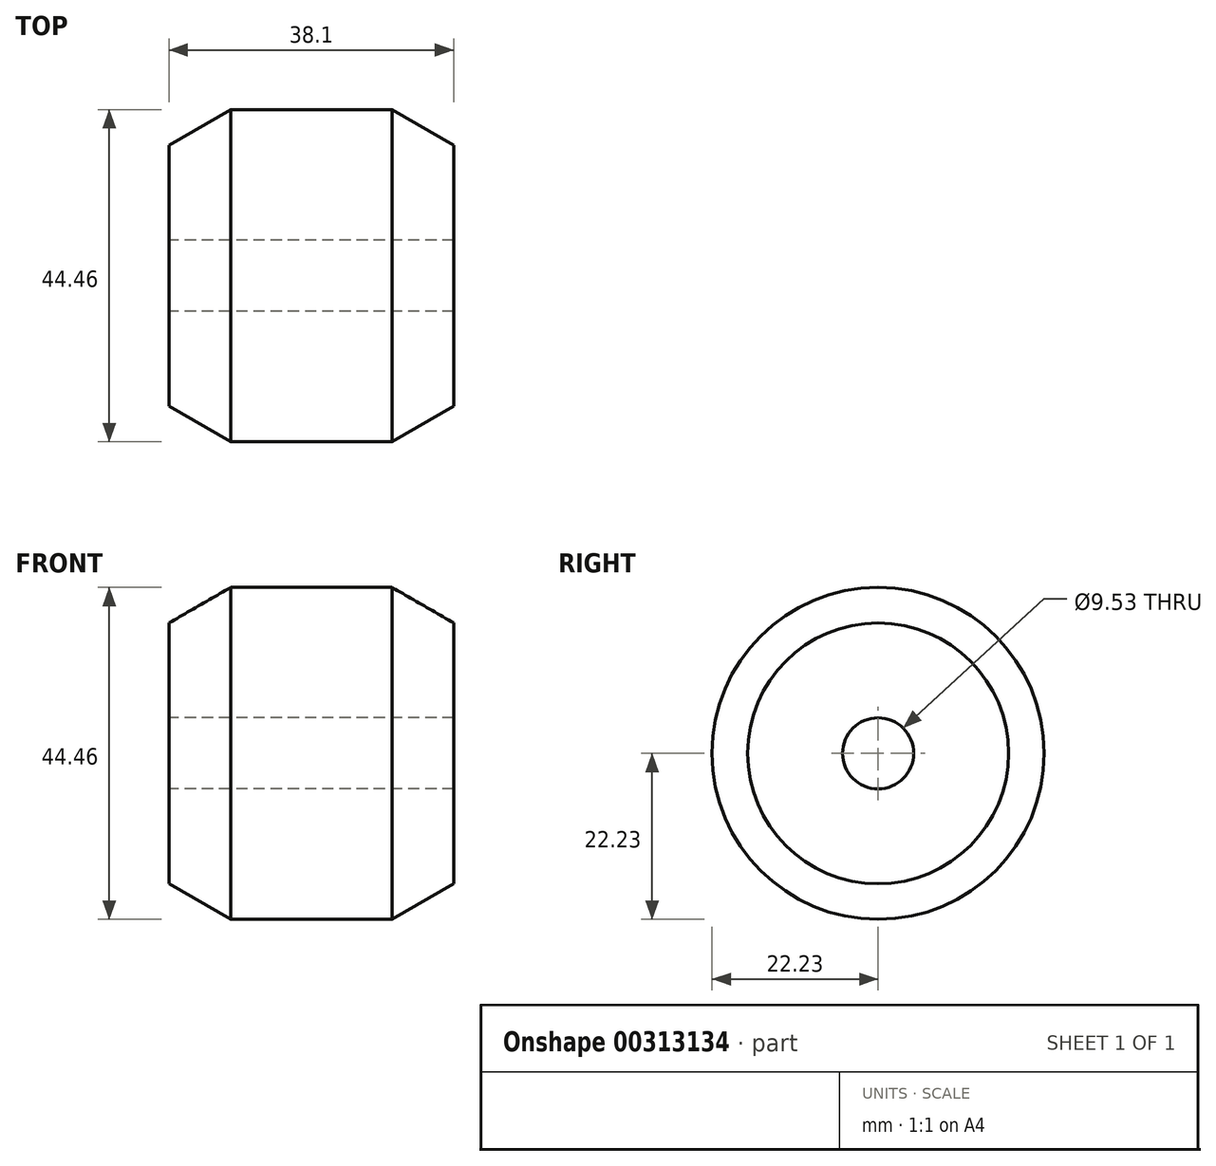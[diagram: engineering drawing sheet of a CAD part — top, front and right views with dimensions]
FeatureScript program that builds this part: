
annotation { "Feature Type Name" : "Feature", "Feature Type Description" : "" }
export const myFeature = defineFeature(function(context is Context, id is Id, definition is map)
    precondition{}
    {
        {
            var Q0;
            Q0=qCreatedBy(makeId("Front.planeOp"),FACE);
            var sketch = newSketch(context, id + "F0", { "sketchPlane" : qUnion([Q0])});
            skLineSegment(sketch, "E0", {"start": v(0, 0) * mm, "end": v(38.1, 0) * mm});
            skLineSegment(sketch, "E1", {"start": v(0, 0) * mm, "end": v(0, 17.46) * mm});
            skLineSegment(sketch, "E2", {"start": v(0, 17.46) * mm, "end": v(8.25, 22.22) * mm});
            skLineSegment(sketch, "E3", {"start": v(8.25, 22.23) * mm, "end": v(29.85, 22.23) * mm});
            skLineSegment(sketch, "E4", {"start": v(29.85, 22.23) * mm, "end": v(38.1, 17.46) * mm});
            skLineSegment(sketch, "E5", {"start": v(38.1, 17.46) * mm, "end": v(38.1, 0) * mm});
            skLineSegment(sketch, "E6", {"start": v(50.8, -38.1) * mm, "end": v(88.9, -38.1) * mm});
            skLineSegment(sketch, "E7", {"start": v(50.8, -38.1) * mm, "end": v(50.8, -20.64) * mm});
            skLineSegment(sketch, "E8", {"start": v(50.8, -20.64) * mm, "end": v(59.05, -15.87) * mm});
            skLineSegment(sketch, "E9", {"start": v(59.05, -15.87) * mm, "end": v(80.65, -15.87) * mm});
            skLineSegment(sketch, "E10", {"start": v(80.65, -15.87) * mm, "end": v(88.9, -20.64) * mm});
            skLineSegment(sketch, "E11", {"start": v(88.9, -20.64) * mm, "end": v(88.9, -38.1) * mm});
            skSolve(sketch);
        }
        {
            var Q0;
            Q0=makeQuery(id+"F0.imprint","IMPRINT",FACE,{"disambiguationData":[TD([[makeQuery(id+"F0.imprint","IMPRINT",EDGE,{"derivedFrom":sQuery(id+"F0.wireOp",EDGE,"E0")}),1.0]])]});
            var Q1;
            Q1=sQuery(id+"F0.wireOp",EDGE,"E0");
            revolve(context, id + "F1", {"entities" : qUnion([Q0]), "axis" : qUnion([Q1]), "revolveType" : RevolveType.FULL});
        }
        {
            var Q0;
            Q0=makeQuery(id+"F1.opRevolve","SWEPT_FACE",FACE,{"disambiguationData":[OSD([sQuery(id+"F0.wireOp",EDGE,"E1")])]});
            var sketch = newSketch(context, id + "F2", { "sketchPlane" : qUnion([Q0])});
            skCircle(sketch, "E12", {"center": v(0, 0) * mm, "radius": 4.76 * mm});
            skCircle(sketch, "E13", {"center": v(0, -38.1) * mm, "radius": 4.76 * mm});
            skSolve(sketch);
        }
        {
            var Q0;
            Q0=qSketchRegion(id+"F2",true);
            extrude(context, id + "F3", {"entities" : qUnion([Q0]), "operationType" : NewBodyOperationType.REMOVE, "endBound" : BoundingType.THROUGH_ALL, "oppositeDirection" : true, "depth" : 25.4 * mm});
        }
    });
